# Revit family: FU_Chair_Sandler_Azure 2-1
name_source: partatom
category: Furniture
units: mm (PartAtom-declared; Revit-internal decimal feet)

## family parameters
Always vertical = Yes
Cut with Voids When Loaded = No
OmniClass Number = 23.40.20.00
OmniClass Title = General Furniture and Specialties
Room Calculation Point = No
Shared = No
Work Plane-Based = No

## types (1)
- Azure 1.1
    Arm Width = 620 mm  [stored 2.03412 ft]
    Default Elevation = 0 mm  [stored 0 ft]
    Depth = 530 mm  [stored 1.73885 ft]
    Description = Armchair with beech frame. Seat and back upholstered. Stacks 8.
    Frame = Wood - Beech - Cherry Wood - V
    Height = 850 mm  [stored 2.78871 ft]
    Manufacturer = Sandler
    Model = Azure 2.1
    URL = https://www.sandlerseating.com
    Upholstery = Fabric - Gravity - Frost CPC32
    Width = 510 mm  [stored 1.67323 ft]

note: [stored X ft] marks values corroborated as IEEE doubles in the binary element streams (Revit-internal decimal feet)

## geometry (parser evidence)
native form markers: Sweep x4
no freeform markers — native parametric forms only
